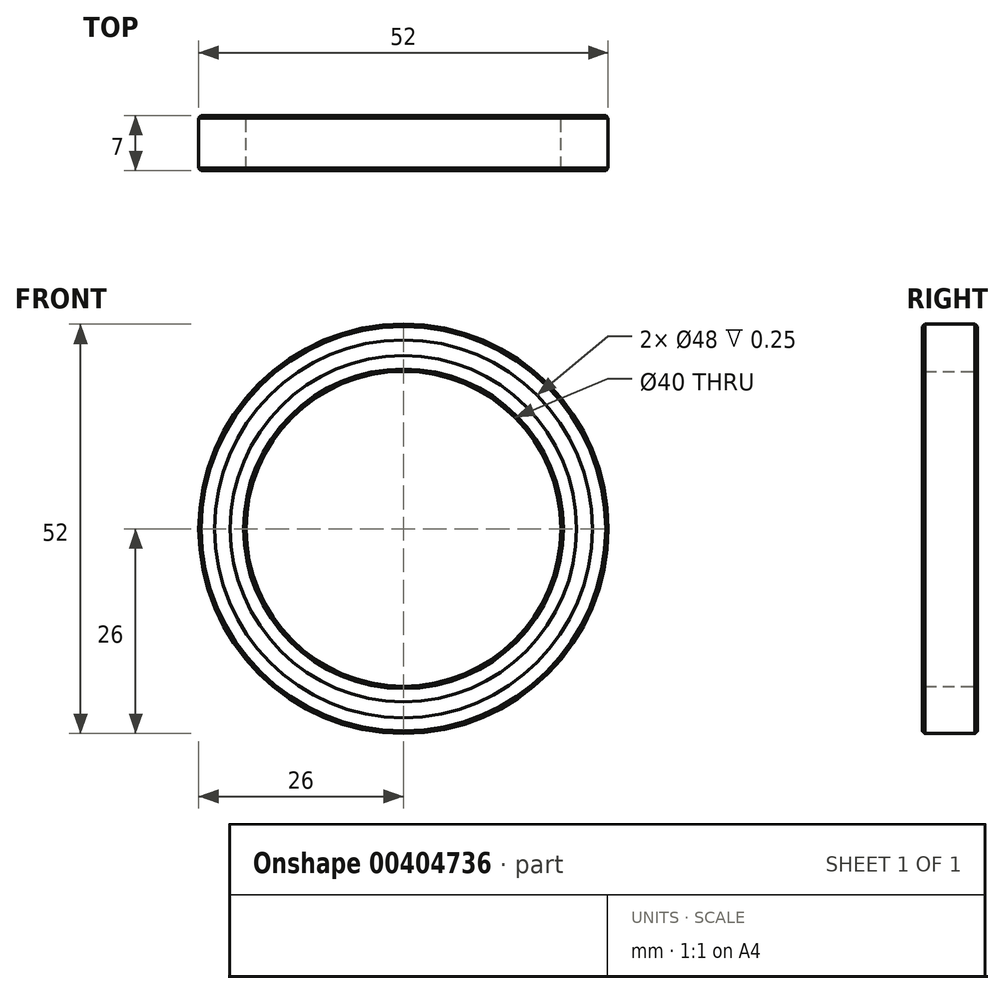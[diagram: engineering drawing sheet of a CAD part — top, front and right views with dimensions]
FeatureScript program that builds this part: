
annotation { "Feature Type Name" : "Feature", "Feature Type Description" : "" }
export const myFeature = defineFeature(function(context is Context, id is Id, definition is map)
    precondition{}
    {
        {
            var Q0;
            Q0=qCreatedBy(makeId("Front.planeOp"),FACE);
            var sketch = newSketch(context, id + "F0", { "sketchPlane" : qUnion([Q0])});
            skCircle(sketch, "E0", {"center": v(0, 0) * mm, "radius": 26 * mm});
            skCircle(sketch, "E1", {"center": v(0, 0) * mm, "radius": 24 * mm});
            skCircle(sketch, "E2", {"center": v(0, 0) * mm, "radius": 22 * mm});
            skCircle(sketch, "E3", {"center": v(0, 0) * mm, "radius": 20 * mm});
            skSolve(sketch);
        }
        {
            var Q0;
            Q0=makeQuery(id+"F0.imprint","IMPRINT",FACE,{"disambiguationData":[TD([[makeQuery(id+"F0.imprint","IMPRINT",EDGE,{"derivedFrom":sQuery(id+"F0.wireOp",EDGE,"E0")}),1.0]])]});
            var Q1;
            Q1=makeQuery(id+"F0.imprint","IMPRINT",FACE,{"disambiguationData":[TD([[makeQuery(id+"F0.imprint","IMPRINT",EDGE,{"derivedFrom":sQuery(id+"F0.wireOp",EDGE,"E2")}),1.0]])]});
            extrude(context, id + "F1", {"entities" : qUnion([Q0, Q1]), "depth" : 7 * mm, "symmetric" : true});
        }
        {
            var Q0;
            Q0=makeQuery(id+"F0.imprint","IMPRINT",FACE,{"disambiguationData":[TD([[makeQuery(id+"F0.imprint","IMPRINT",EDGE,{"derivedFrom":sQuery(id+"F0.wireOp",EDGE,"E1")}),1.0]])]});
            extrude(context, id + "F2", {"entities" : qUnion([Q0]), "operationType" : NewBodyOperationType.ADD, "depth" : 6.5 * mm, "symmetric" : true});
        }
        {
            var Q0;
            Q0=makeQuery(id+"F1.opExtrude","CAP_EDGE",EDGE,{"disambiguationData":[OSD([sQuery(id+"F0.wireOp",EDGE,"E0")])],"isStart":false});
            var Q1;
            Q1=makeQuery(id+"F1.opExtrude","CAP_EDGE",EDGE,{"disambiguationData":[OSD([sQuery(id+"F0.wireOp",EDGE,"E0")])],"isStart":true});
            var Q2;
            Q2=makeQuery(id+"F1.opExtrude","CAP_EDGE",EDGE,{"disambiguationData":[OSD([sQuery(id+"F0.wireOp",EDGE,"E3")])],"isStart":false});
            var Q3;
            Q3=makeQuery(id+"F1.opExtrude","CAP_EDGE",EDGE,{"disambiguationData":[OSD([sQuery(id+"F0.wireOp",EDGE,"E3")])],"isStart":true});
            chamfer(context, id + "F3", {"entities" : qUnion([Q0, Q1, Q2, Q3]), "width" : .3 * mm, "tangentPropagation" : true});
        }
    });
